# Revit family: IS_StradaO_K0784_BIM_DE
name_source: partatom
category: Plumbing Fixtures
revit_build: Autodesk Revit MEP 2016 (Build: 20161004_0715(x64)
units: mm (PartAtom-declared; Revit-internal decimal feet)

## family parameters
Always vertical = No
Cut with Voids When Loaded = No
OmniClass Number = 23.45.05.14.14
OmniClass Title = Sinks/Lavatories
Part Type = Normal
Room Calculation Point = No
Round Connector Dimension = Use Diameter
Shared = No
Work Plane-Based = No

## types (2) — shared parameters
Accessories = www.idealstandard.de\ersatzteile
AssetType = Fixed
BIMobject category = Basins
BOSUseNativeGeometries = 1
Brand = Ideal Standard
Brand url = http://www.idealstandard.de
CodePerformance = DIN EN 14688 CL 20, DIN EN 31
ConnectionType = Plumbing
CurrencyUnit = €
CurrentRevision = 1
DurationUnit = Jaar
EAN code = https://4015413040419
Edition number = 1
ExpectedLife = 25
Features = STRADA O vessel basin 600x420mm, no taphole, no overflow
IFC Classification = Sanitary Terminal
IfcExportAs = Sanitary terminal type
IfcExportType = WASHBASIN
Installation instructions = http://www.idealstandard.de
InstallationInstructions = www.idealstandard.de\produkte
LinearUnits = millimetres
MaintenanceInformation = www.idealstandard.de
Manufacturer = http://www.idealstandard.de
Manufacturer name = Ideal Standard
ManufacturerURL = http://www.idealstandard.de
Material = Vitreous china
Material main = Ceramics
Nominal height = 160
Nominal width = 600
NominalHeight = 160 mm  [stored 0.524934 ft]
NominalLength = 426 mm
NominalWidth = 602 mm
Product Guid = 7e4850be-9397-4873-b4bd-dd1641ca86fc
Product SKU = K0784
Product certification = DIN EN 14688 CL 20, DIN EN 31
Product data url = https://bimobject.com
Product family = STRADA O
Product group = Basin
Product name = STRADA O vessel basin 600x420mm, no taphole, no overflow
Product url = http://www.idealstandard.de
ProductInformation = www.idealstandard.de/produkte
QR code = http://bimobject.com
Shape = Sculptured
Size = 602x426x160 mm
Space = Internal
SpareParts = www.idealstandard.de/ersatzteile
Technical description = http://www.idealstandard.de
URL = http://www.idealstandard.de
Uniclass2015Code = Pr_40_20_96_18
Uniclass2015Title = Counter top wash basins
Uniclass2015Version = Products v1.1
VolumeUnits = Litres
WashHandBasinMounting = Countertop
WashHandBasinType = Hand Rinse
Weight Net (Kg) = 13
zero-valued in all types: Cost, DrainSize

## per-type parameters (varying)
| type | BIMObjectName | BarCode | Color | Finish | MainColor | Model | ModelNumber | Name | NettWeight |
| K078401 STRADA O vessel basin 600x420mm, no taphole, no overflow | ISI_IdealStandard_CounterTopWashbasins_STRADA_K078401 | 4015413040419 | White | White | White | K078401 | K078401 | ISI_IdealStandard_CounterTopWashbasins_STRADA_K078401 | 13 kg |
| K0784MA STRADA O vessel basin 600x420mm, no taphole, no overflow | ISI_IdealStandard_CounterTopWashbasins_STRADA_K0784MA | 4015413040426 | WHITE IP | WHITE IP | WHITE IP | K0784MA | K0784MA | ISI_IdealStandard_CounterTopWashbasins_STRADA_K0784MA | 15 kg |

note: column(s) folded — value = type name in every type: Description, ModelReference

note: [stored X ft] marks values corroborated as IEEE doubles in the binary element streams (Revit-internal decimal feet)

## geometry (parser evidence)
native form markers: Blend x4, Sweep x1
no freeform markers — native parametric forms only
